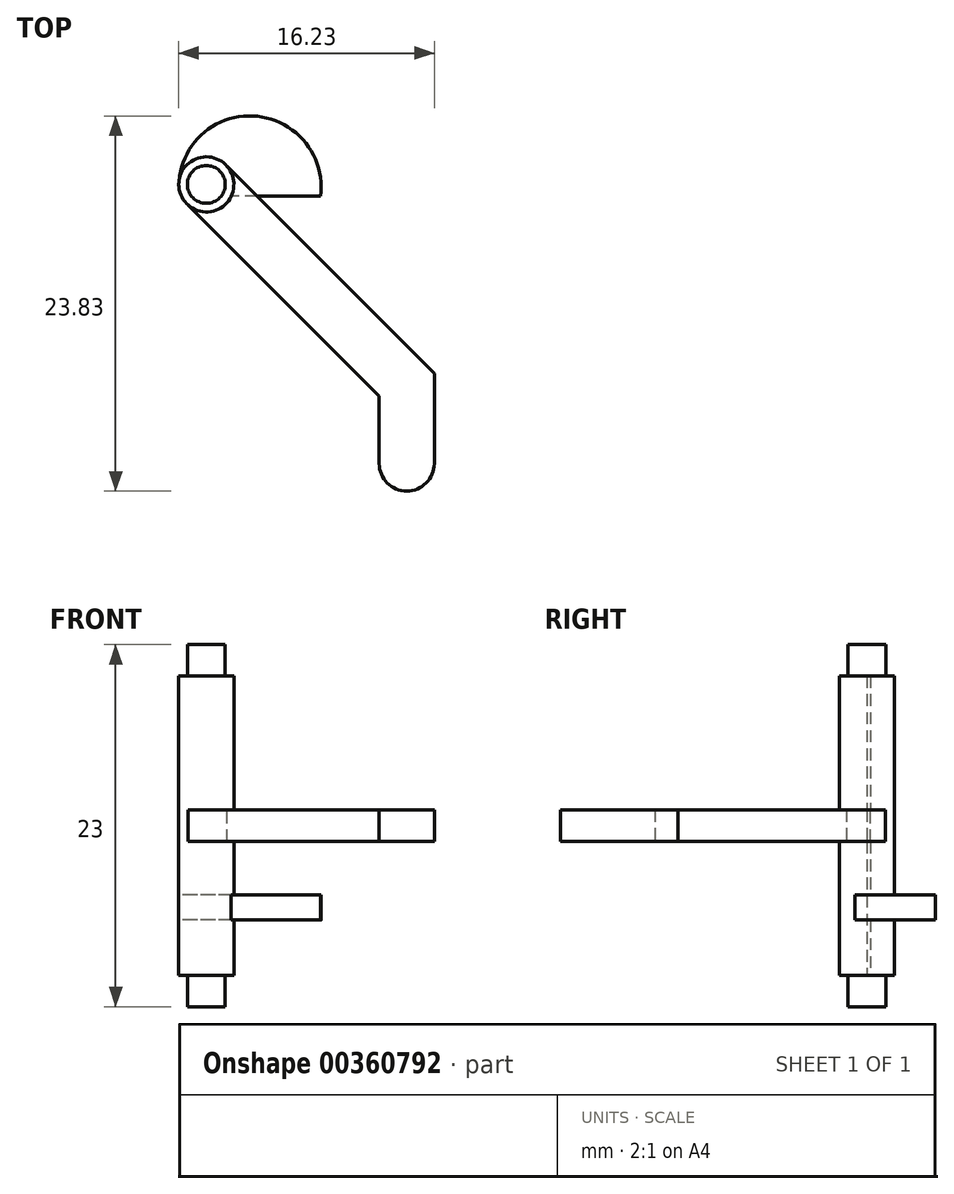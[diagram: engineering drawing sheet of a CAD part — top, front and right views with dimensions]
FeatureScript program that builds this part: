
annotation { "Feature Type Name" : "Feature", "Feature Type Description" : "" }
export const myFeature = defineFeature(function(context is Context, id is Id, definition is map)
    precondition{}
    {
        {
            var Q0;
            Q0=qCreatedBy(makeId("Top.planeOp"),FACE);
            var sketch = newSketch(context, id + "F0", { "sketchPlane" : qUnion([Q0])});
            skCircle(sketch, "E0", {"center": v(0, 0) * mm, "radius": 1.75 * mm});
            skCircle(sketch, "E1", {"center": v(0, 0) * mm, "radius": 1.2 * mm});
            skArc(sketch, "E2", {"start": v(7.25, -0.75) * mm, "mid": v(3.14, 4.33) * mm, "end": v(-1.75, 0) * mm});
            skLineSegment(sketch, "E3", {"start": v(7.25, -0.75) * mm, "end": v(1.58, -0.75) * mm});
            skSolve(sketch);
        }
        {
            var Q0;
            Q0=makeQuery(id+"F0.imprint","IMPRINT",FACE,{"disambiguationData":[TD([[makeQuery(id+"F0.imprint","IMPRINT",EDGE,{"derivedFrom":sQuery(id+"F0.wireOp",EDGE,"E1")}),1.0]])]});
            extrude(context, id + "F1", {"entities" : qUnion([Q0]), "depth" : 17.5 * mm, "hasSecondDirection" : true, "secondDirectionOppositeDirection" : true, "secondDirectionDepth" : 5.5 * mm});
        }
        {
            var Q0;
            Q0=makeQuery(id+"F0.imprint","IMPRINT",FACE,{"disambiguationData":[TD([[makeQuery(id+"F0.imprint","IMPRINT",EDGE,{"derivedFrom":sQuery(id+"F0.wireOp",EDGE,"E0")}),1.0]])]});
            extrude(context, id + "F2", {"entities" : qUnion([Q0]), "operationType" : NewBodyOperationType.ADD, "depth" : 15.5 * mm, "hasSecondDirection" : true, "secondDirectionOppositeDirection" : true, "secondDirectionDepth" : 3.5 * mm});
        }
        {
            var Q0;
            {var subQ0=sQuery(id+"F0.wireOp",EDGE,"E3");Q0=makeQuery(id+"F0.imprint","IMPRINT",FACE,{"disambiguationData":[TD([[makeQuery(id+"F0.imprint","IMPRINT",EDGE,{"derivedFrom":subQ0}),-1.0]])]});}
            extrude(context, id + "F3", {"entities" : qUnion([Q0]), "operationType" : NewBodyOperationType.ADD, "depth" : 1.6 * mm});
        }
        {
            var Q0;
            Q0=qCreatedBy(makeId("Top.planeOp"),FACE);
            cPlane(context, id + "F4", {"entities" : qUnion([Q0]), "cplaneType" : CPlaneType.OFFSET, "offset" : 6 * mm, "width" : 150 * mm, "height" : 150 * mm});
        }
        {
            var Q0;
            Q0=qCreatedBy(id+"F4.planeOp",FACE);
            var sketch = newSketch(context, id + "F5", { "sketchPlane" : qUnion([Q0])});
            skLineSegment(sketch, "E4", {"start": v(0, 0) * mm, "end": v(12.73, -12.73) * mm, "construction": true});
            skLineSegment(sketch, "E5", {"start": v(1.3, 1.16) * mm, "end": v(14.48, -12) * mm});
            skLineSegment(sketch, "E6", {"start": v(-1.2, -1.28) * mm, "end": v(10.98, -13.45) * mm});
            skLineSegment(sketch, "E7", {"start": v(12.73, -12.73) * mm, "end": v(12.73, -17.73) * mm, "construction": true});
            skCircle(sketch, "E8", {"center": v(12.73, -17.73) * mm, "radius": 1.75 * mm});
            skLineSegment(sketch, "E9", {"start": v(10.98, -17.73) * mm, "end": v(10.98, -13.45) * mm});
            skLineSegment(sketch, "E10", {"start": v(14.48, -17.73) * mm, "end": v(14.48, -12) * mm});
            skCircle(sketch, "E11", {"center": v(0, 0) * mm, "radius": 1.75 * mm});
            skSolve(sketch);
        }
        {
            var Q0;
            Q0 = qSketchRegion(id + "F5", true);
            extrude(context, id + "F6", {"entities" : qUnion([Q0]), "operationType" : NewBodyOperationType.ADD, "depth" : 1 * mm, "offsetDistance" : 25 * mm, "hasSecondDirection" : true, "secondDirectionOppositeDirection" : true, "secondDirectionDepth" : 1 * mm});
        }
    });
